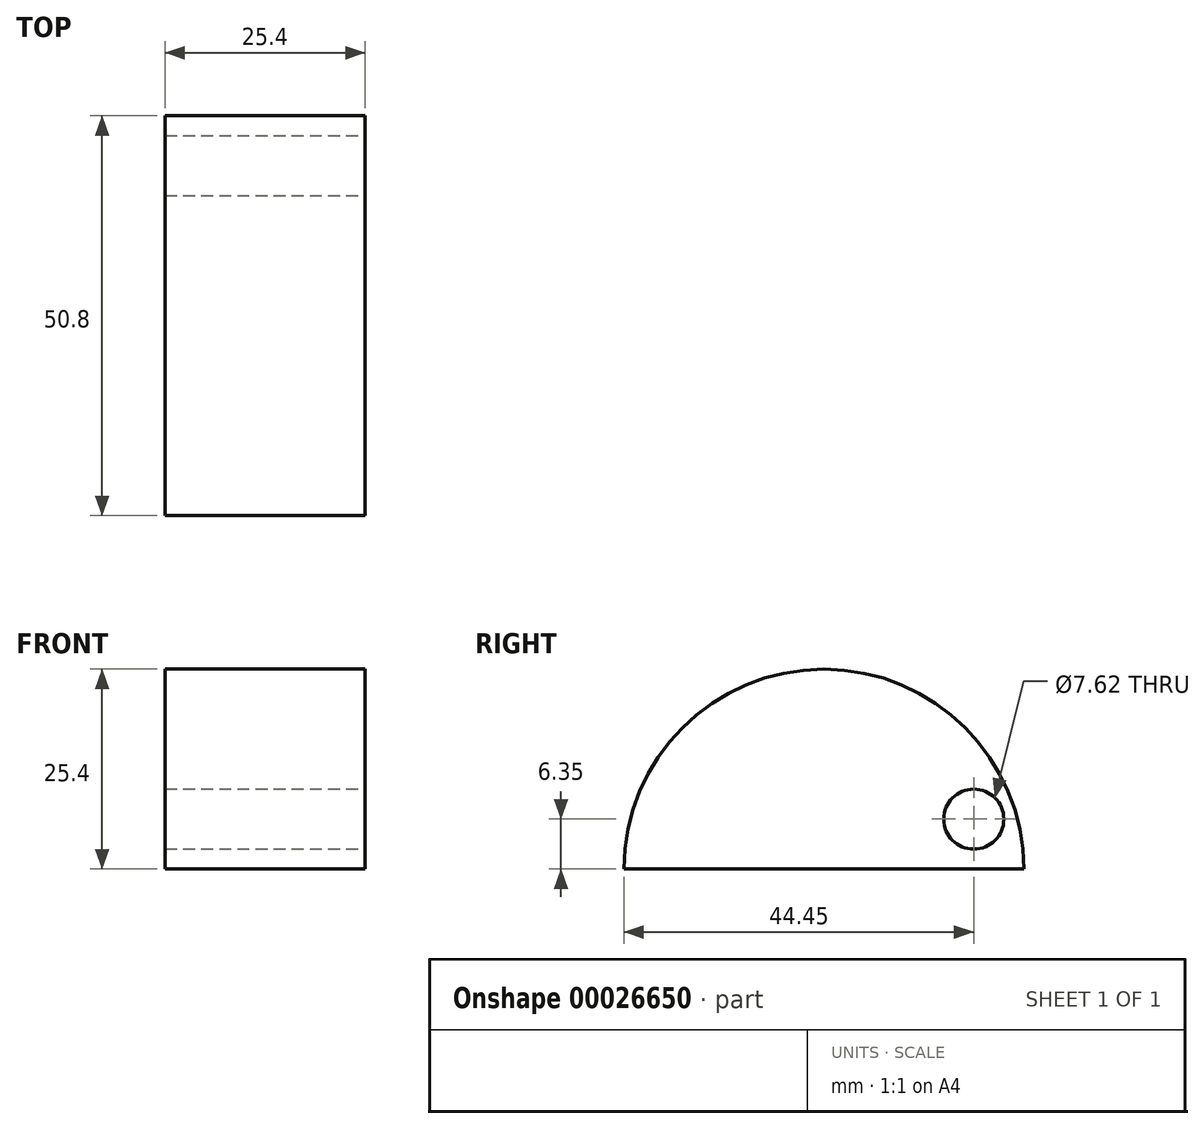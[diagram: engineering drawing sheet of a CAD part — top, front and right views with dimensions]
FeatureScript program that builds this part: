
annotation { "Feature Type Name" : "Feature", "Feature Type Description" : "" }
export const myFeature = defineFeature(function(context is Context, id is Id, definition is map)
    precondition{}
    {
        {
            var Q0;
            Q0=qCreatedBy(makeId("Front.planeOp"),FACE);
            var sketch = newSketch(context, id + "F0", { "sketchPlane" : qUnion([Q0])});
            skLineSegment(sketch, "E0.bottom", {"start": v(-6.71, 0) * mm, "end": v(18.69, 0) * mm});
            skLineSegment(sketch, "E0.top", {"start": v(-6.71, -25.4) * mm, "end": v(18.69, -25.4) * mm});
            skLineSegment(sketch, "E0.left", {"start": v(-6.71, 0) * mm, "end": v(-6.71, -25.4) * mm});
            skLineSegment(sketch, "E0.right", {"start": v(18.69, 0) * mm, "end": v(18.69, -25.4) * mm});
            skSolve(sketch);
        }
        {
            var Q0;
            Q0=makeQuery(id+"F0.imprint","IMPRINT",FACE,{"disambiguationData":[TD([[makeQuery(id+"F0.imprint","IMPRINT",EDGE,{"derivedFrom":sQuery(id+"F0.wireOp",EDGE,"E0.bottom")}),-1.0]])]});
            var Q1;
            Q1=sQuery(id+"F0.wireOp",EDGE,"E0.top");
            revolve(context, id + "F1", {"entities" : qUnion([Q0]), "axis" : qUnion([Q1]), "revolveType" : RevolveType.SYMMETRIC, "angle" : 180 * degree});
        }
        {
            var Q0;
            Q0=makeQuery(id+"F1.opRevolve","SWEPT_FACE",FACE,{"disambiguationData":[OSD([sQuery(id+"F0.wireOp",EDGE,"E0.right")])]});
            var sketch = newSketch(context, id + "F2", { "sketchPlane" : qUnion([Q0])});
            skLineSegment(sketch, "E1", {"start": v(0, 0) * mm, "end": v(0, -25.4) * mm});
            skLineSegment(sketch, "E2", {"start": v(0, 0) * mm, "end": v(25.4, -25.4) * mm});
            skPoint(sketch, "E3", {"position": v(12.7, -12.7) * mm});
            skLineSegment(sketch, "E4", {"start": v(12.7, -12.7) * mm, "end": v(12.7, -25.4) * mm});
            skLineSegment(sketch, "E5", {"start": v(12.7, -25.4) * mm, "end": v(19.05, -19.05) * mm});
            skCircle(sketch, "E6", {"center": v(19.05, -19.05) * mm, "radius": 3.81 * mm});
            skSolve(sketch);
        }
        {
            var Q0;
            {var subQ1=sQuery(id+"F2.wireOp",EDGE,"E2");var subQ4=makeQuery(id+"F2.imprint","INTERSECT",VERTEX,{"derivedFrom":[subQ1,sQuery(id+"F2.wireOp",EDGE,"E5")]});Q0=makeQuery(id+"F2.imprint","IMPRINT",FACE,{"disambiguationData":[TD([[makeQuery(id+"F2.imprint","IMPRINT",EDGE,{"disambiguationData":[TD([[subQ4,1.0]])],"derivedFrom":subQ1}),1.0]])]});}
            extrude(context, id + "F3", {"entities" : qUnion([Q0]), "operationType" : NewBodyOperationType.REMOVE, "endBound" : BoundingType.THROUGH_ALL, "oppositeDirection" : true, "depth" : 25.4 * mm});
        }
        {
            var Q0;
            {var subQ1=sQuery(id+"F2.wireOp",EDGE,"E5");var subQ3=sQuery(id+"F2.wireOp",EDGE,"E2");var subQ5=makeQuery(id+"F2.imprint","INTERSECT",VERTEX,{"derivedFrom":[subQ3,subQ1]});Q0=makeQuery(id+"F2.imprint","IMPRINT",FACE,{"disambiguationData":[TD([[makeQuery(id+"F2.imprint","IMPRINT",EDGE,{"disambiguationData":[TD([[subQ5,1.0]])],"derivedFrom":subQ3}),-1.0]])]});}
            extrude(context, id + "F4", {"entities" : qUnion([Q0]), "operationType" : NewBodyOperationType.REMOVE, "endBound" : BoundingType.THROUGH_ALL, "oppositeDirection" : true, "depth" : 25.4 * mm});
        }
        {
            var Q0;
            {var subQ1=sQuery(id+"F2.wireOp",EDGE,"E5");var subQ3=sQuery(id+"F2.wireOp",EDGE,"E2");var subQ5=makeQuery(id+"F2.imprint","INTERSECT",VERTEX,{"derivedFrom":[subQ3,subQ1]});Q0=makeQuery(id+"F2.imprint","IMPRINT",FACE,{"disambiguationData":[TD([[makeQuery(id+"F2.imprint","IMPRINT",EDGE,{"disambiguationData":[TD([[subQ5,-1.0]])],"derivedFrom":subQ3}),-1.0]])]});}
            extrude(context, id + "F5", {"entities" : qUnion([Q0]), "operationType" : NewBodyOperationType.REMOVE, "endBound" : BoundingType.THROUGH_ALL, "oppositeDirection" : true, "depth" : 25.4 * mm});
        }
    });
